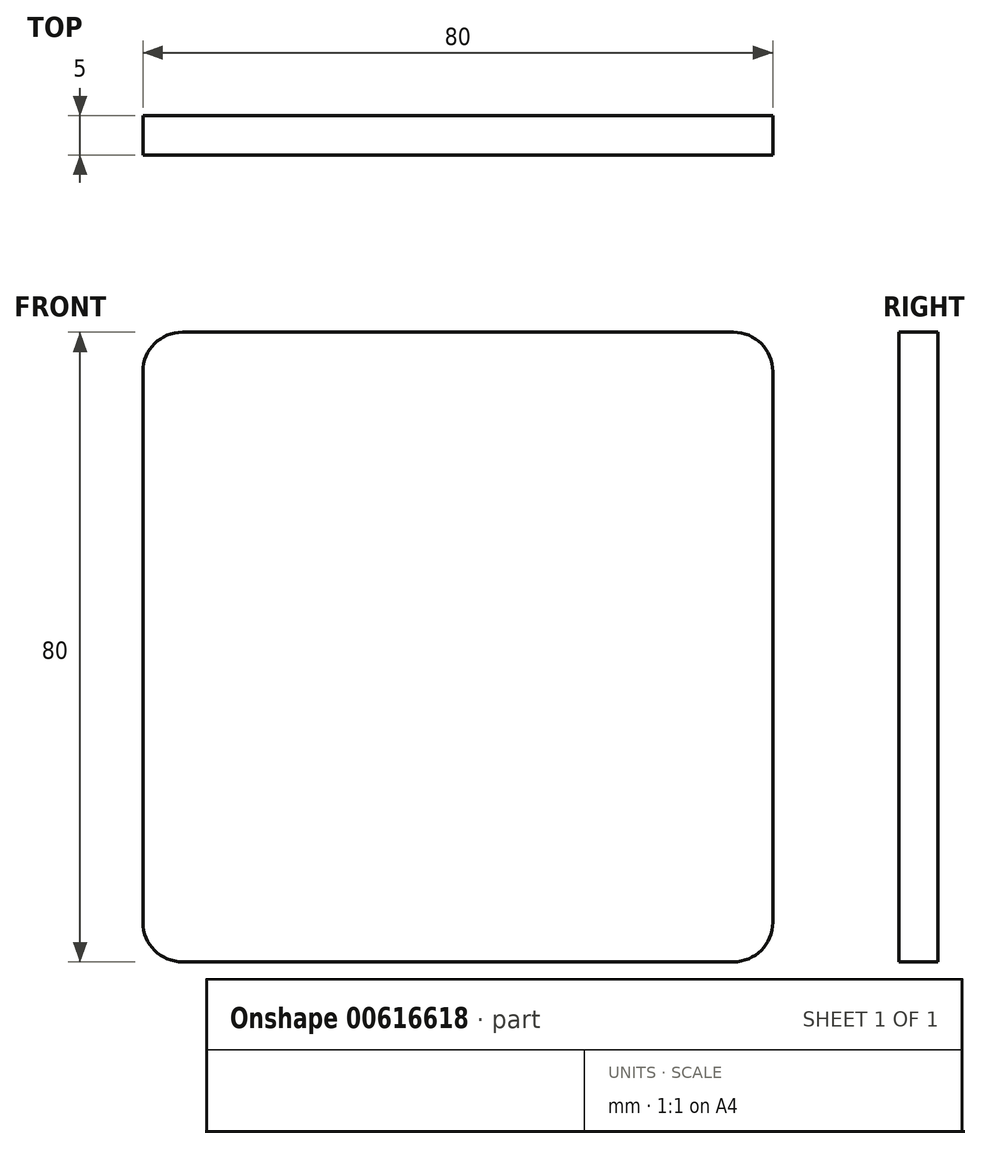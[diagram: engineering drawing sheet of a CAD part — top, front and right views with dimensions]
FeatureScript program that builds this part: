
annotation { "Feature Type Name" : "Feature", "Feature Type Description" : "" }
export const myFeature = defineFeature(function(context is Context, id is Id, definition is map)
    precondition{}
    {
        {
            var Q0;
            Q0=qCreatedBy(makeId("Front.planeOp"),FACE);
            var sketch = newSketch(context, id + "F0", { "sketchPlane" : qUnion([Q0])});
            skLineSegment(sketch, "E0.bottom", {"start": v(-23.98, 98.54) * mm, "end": v(46.02, 98.54) * mm});
            skLineSegment(sketch, "E0.top", {"start": v(-23.98, 18.54) * mm, "end": v(46.02, 18.54) * mm});
            skLineSegment(sketch, "E0.left", {"start": v(-28.98, 93.54) * mm, "end": v(-28.98, 23.54) * mm});
            skLineSegment(sketch, "E0.right", {"start": v(51.02, 93.54) * mm, "end": v(51.02, 23.54) * mm});
            skPoint(sketch, "E1.visualSharp", {"position": v(-28.98, 98.54) * mm});
            skArc(sketch, "E1.filletArc", {"start": v(-23.98, 98.54) * mm, "mid": v(-27.52, 97.07) * mm, "end": v(-28.98, 93.54) * mm});
            skPoint(sketch, "E2.visualSharp", {"position": v(51.02, 98.54) * mm});
            skArc(sketch, "E2.filletArc", {"start": v(51.02, 93.54) * mm, "mid": v(49.55, 97.07) * mm, "end": v(46.02, 98.54) * mm});
            skPoint(sketch, "E3.visualSharp", {"position": v(51.02, 18.54) * mm});
            skArc(sketch, "E3.filletArc", {"start": v(46.02, 18.54) * mm, "mid": v(49.55, 20) * mm, "end": v(51.02, 23.54) * mm});
            skPoint(sketch, "E4.visualSharp", {"position": v(-28.98, 18.54) * mm});
            skArc(sketch, "E4.filletArc", {"start": v(-28.98, 23.54) * mm, "mid": v(-27.52, 20) * mm, "end": v(-23.98, 18.54) * mm});
            skSolve(sketch);
        }
        {
            var Q0;
            Q0 = qSketchRegion(id + "F0", true);
            extrude(context, id + "F1", {"entities" : qUnion([Q0]), "depth" : 5 * mm, "offsetDistance" : 25 * mm});
        }
    });
